# Revit family: Sink-Corian-European-Salty-9410
name_source: partatom
category: Plumbing Fixtures
revit_build: Autodesk Revit 2015 (Build: 20140606_1530(x64)
units: mm (PartAtom-declared; Revit-internal decimal feet)

## types (1)
- 9410
    CWFU = 0
    Cost = 0 $
    Default Elevation = 1219 mm
    Depth = 176 mm  [stored 0.577428 ft]
    Description = Kitchen Sink Europe Specification
    Finish = Solid Surface Sink - DuPont - Glacier White
    HWFU = 0
    Interior Length = 400 mm  [stored 1.31234 ft]
    Interior Width = 800 mm  [stored 2.62467 ft]
    Length = 450 mm  [stored 1.47638 ft]
    Manufacturer = DuPont
    Model = Salty 9410
    Product Page URL = http://www.corian.uk
    Sink Colors Available = Designer White, Glacier White
    URL = http://www.corian.uk
    Version = 2015 - v1.0b
    WFU = 0
    Width = 850 mm  [stored 2.78871 ft]

note: [stored X ft] marks values corroborated as IEEE doubles in the binary element streams (Revit-internal decimal feet)

## geometry (parser evidence)
native form markers: Sweep x2
no freeform markers — native parametric forms only
